# Revit family: Screens-Mounted-Teknion-JNSEGB-Glass_Elevated-R20161
name_source: partatom
category: Furniture
revit_build: Autodesk Revit Architecture 2016 (Build: 20150714_1515(x64)
units: mm (PartAtom-declared; Revit-internal decimal feet)

## family parameters
Always vertical = Yes
Cut with Voids When Loaded = No
OmniClass Number = 23.40.20.00
OmniClass Title = General Furniture and Specialties
Room Calculation Point = No
Shared = Yes
Work Plane-Based = No

## types (4) — shared parameters
Assembly Code = E2020200
Manufacturer = Teknion
Manufacturer Fax = 416.661.4586
Part Number = JNSEGB
Product Documentation Link = https://www.teknion.com
Product Line = Expansion Cityline
Product Page URL = http://www.teknion.com
Series = Expansion Cityline
Sustainability Data = http://www.teknion.com
URL = www.teknion.com
Unit Weight URL = http://www.teknion.com
Warranty = http://www.teknion.com

## per-type parameters (varying)
| type | Both Side | Description | Model | Side A | Side B |
| Standard Width | No | Glass Elevated Screen - Beam Mounted, 10" Modesty Base Height, Standard Width, Standard Corner Detail | JNSEGB10__SS | No | No |
| One Side - Left | No | Glass Elevated Screen - Beam Mounted, 10" Modesty Base Height, Left Side Width Extension, Standard Corner Detail | JNSEGB10__LS | Yes | No |
| Both Side | Yes | Glass Elevated Screen - Beam Mounted, 10" Modesty Base Height, Both Sides Width Extension, Standard Corner Detail | JNSEGB10__BS | No | No |
| One Side - Right | No | Glass Elevated Screen - Beam Mounted, 10" Modesty Base Height, Right Side Width Extension, Standard Corner Detail | JNSEGB10__RS | No | Yes |

type visibility flags (boolean, named after types; folded from table):
- Standard Width: Yes: Standard Width
- One Side - Left: Yes: (none)
- Both Side: Yes: (none)
- One Side - Right: Yes: (none)

## geometry (parser evidence)
native form markers: Sweep x2
no freeform markers — native parametric forms only
